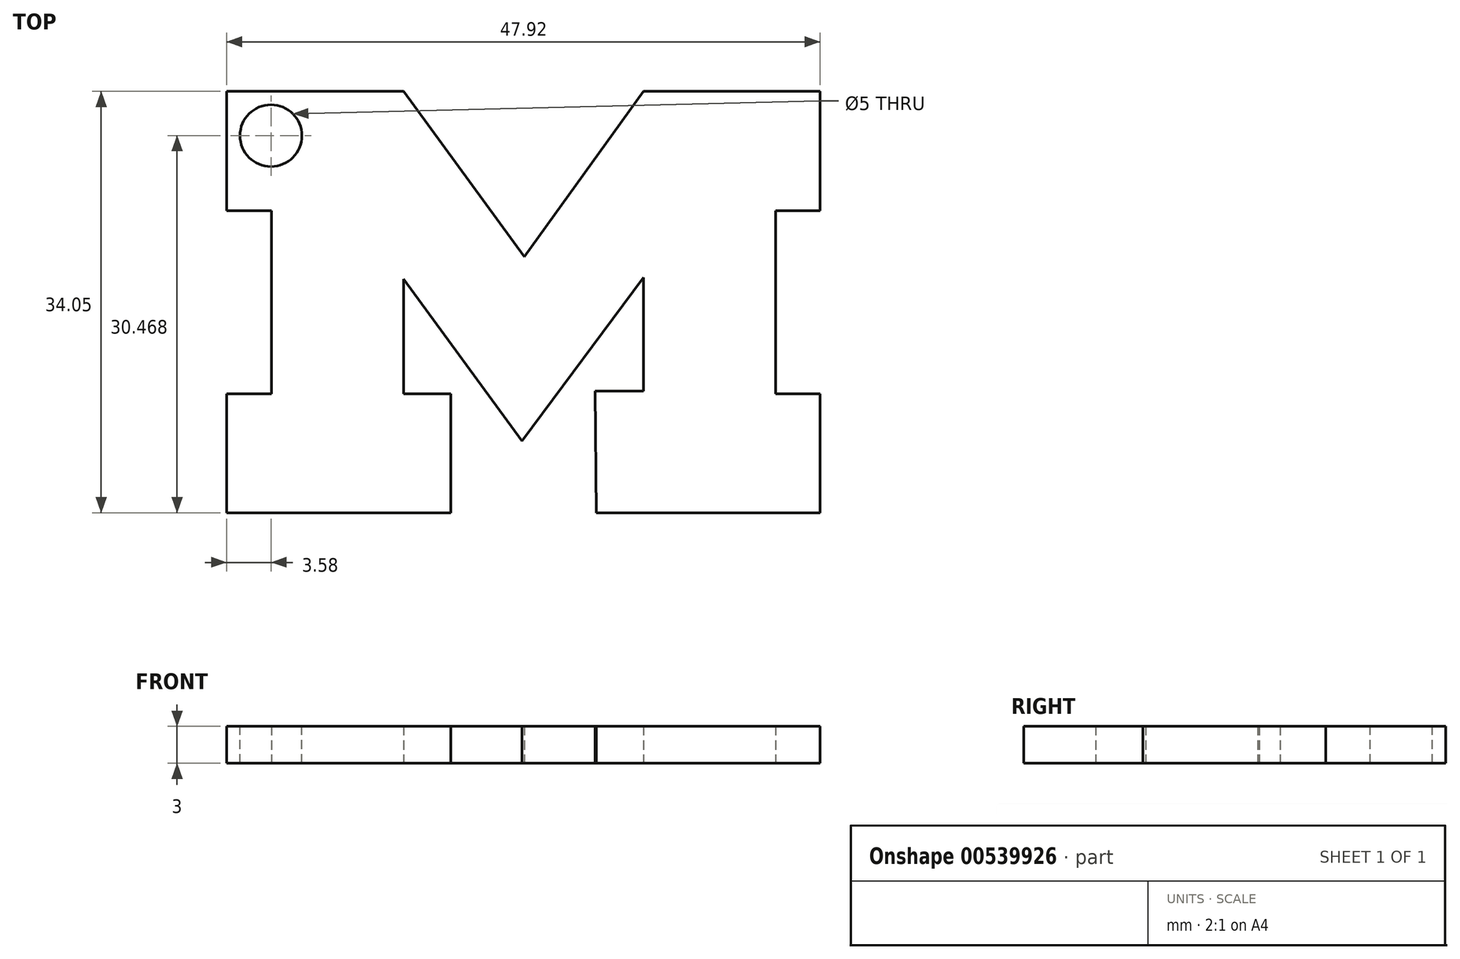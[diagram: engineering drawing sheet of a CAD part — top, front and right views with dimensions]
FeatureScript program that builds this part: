
annotation { "Feature Type Name" : "Feature", "Feature Type Description" : "" }
export const myFeature = defineFeature(function(context is Context, id is Id, definition is map)
    precondition{}
    {
        {
            var Q0;
            Q0=qCreatedBy(makeId("Top.planeOp"),FACE);
            var sketch = newSketch(context, id + "F0", { "sketchPlane" : qUnion([Q0])});
            skLineSegment(sketch, "E0", {"start": v(39.47, 27.3) * mm, "end": v(57.55, 27.3) * mm});
            skLineSegment(sketch, "E1", {"start": v(57.55, 27.3) * mm, "end": v(57.55, 36.88) * mm});
            skLineSegment(sketch, "E2", {"start": v(57.55, 36.88) * mm, "end": v(53.97, 36.88) * mm});
            skLineSegment(sketch, "E3", {"start": v(53.97, 36.88) * mm, "end": v(53.97, 51.68) * mm});
            skLineSegment(sketch, "E4", {"start": v(53.97, 51.68) * mm, "end": v(57.55, 51.68) * mm});
            skLineSegment(sketch, "E5", {"start": v(57.55, 51.68) * mm, "end": v(57.55, 61.34) * mm});
            skLineSegment(sketch, "E6", {"start": v(57.55, 61.34) * mm, "end": v(43.29, 61.34) * mm});
            skLineSegment(sketch, "E7", {"start": v(43.29, 61.34) * mm, "end": v(33.67, 48) * mm});
            skLineSegment(sketch, "E8", {"start": v(33.67, 48) * mm, "end": v(23.93, 61.34) * mm});
            skLineSegment(sketch, "E9", {"start": v(23.93, 61.34) * mm, "end": v(9.63, 61.34) * mm});
            skLineSegment(sketch, "E10", {"start": v(9.63, 61.34) * mm, "end": v(9.63, 51.68) * mm});
            skLineSegment(sketch, "E11", {"start": v(9.63, 51.68) * mm, "end": v(13.25, 51.68) * mm});
            skLineSegment(sketch, "E12", {"start": v(13.25, 51.68) * mm, "end": v(13.25, 36.88) * mm});
            skLineSegment(sketch, "E13", {"start": v(13.25, 36.88) * mm, "end": v(9.63, 36.88) * mm});
            skLineSegment(sketch, "E14", {"start": v(9.63, 36.88) * mm, "end": v(9.63, 27.3) * mm});
            skLineSegment(sketch, "E15", {"start": v(9.63, 27.3) * mm, "end": v(27.74, 27.3) * mm});
            skLineSegment(sketch, "E16", {"start": v(27.74, 27.3) * mm, "end": v(27.74, 36.88) * mm});
            skLineSegment(sketch, "E17", {"start": v(27.74, 36.88) * mm, "end": v(23.93, 36.88) * mm});
            skLineSegment(sketch, "E18", {"start": v(23.93, 36.88) * mm, "end": v(23.93, 46.16) * mm});
            skLineSegment(sketch, "E19", {"start": v(23.93, 46.16) * mm, "end": v(33.47, 33.1) * mm});
            skLineSegment(sketch, "E20", {"start": v(33.47, 33.1) * mm, "end": v(43.29, 46.28) * mm});
            skLineSegment(sketch, "E21", {"start": v(43.29, 46.28) * mm, "end": v(43.29, 37.12) * mm});
            skLineSegment(sketch, "E22", {"start": v(43.29, 37.12) * mm, "end": v(39.4, 37.12) * mm});
            skLineSegment(sketch, "E23", {"start": v(39.4, 37.12) * mm, "end": v(39.47, 27.3) * mm});
            skSolve(sketch);
        }
        {
            var Q0;
            Q0=makeQuery(id+"F0.imprint","IMPRINT",FACE,{"disambiguationData":[TD([[makeQuery(id+"F0.imprint","IMPRINT",EDGE,{"derivedFrom":sQuery(id+"F0.wireOp",EDGE,"E0")}),1.0]])]});
            extrude(context, id + "F1", {"entities" : qUnion([Q0]), "depth" : 3 * mm, "offsetDistance" : 25.4 * mm});
        }
        {
            var Q0;
            Q0=makeQuery(id+"F1.opExtrude","CAP_FACE",FACE,{"disambiguationData":[OSD([sQuery(id+"F0.wireOp",EDGE,"E0"),sQuery(id+"F0.wireOp",EDGE,"E1"),sQuery(id+"F0.wireOp",EDGE,"E2"),sQuery(id+"F0.wireOp",EDGE,"E3"),sQuery(id+"F0.wireOp",EDGE,"E4"),sQuery(id+"F0.wireOp",EDGE,"E5"),sQuery(id+"F0.wireOp",EDGE,"E6"),sQuery(id+"F0.wireOp",EDGE,"E7"),sQuery(id+"F0.wireOp",EDGE,"E8"),sQuery(id+"F0.wireOp",EDGE,"E9"),sQuery(id+"F0.wireOp",EDGE,"E10"),sQuery(id+"F0.wireOp",EDGE,"E11"),sQuery(id+"F0.wireOp",EDGE,"E12"),sQuery(id+"F0.wireOp",EDGE,"E13"),sQuery(id+"F0.wireOp",EDGE,"E14"),sQuery(id+"F0.wireOp",EDGE,"E15"),sQuery(id+"F0.wireOp",EDGE,"E16"),sQuery(id+"F0.wireOp",EDGE,"E17"),sQuery(id+"F0.wireOp",EDGE,"E18"),sQuery(id+"F0.wireOp",EDGE,"E19"),sQuery(id+"F0.wireOp",EDGE,"E20"),sQuery(id+"F0.wireOp",EDGE,"E21"),sQuery(id+"F0.wireOp",EDGE,"E22"),sQuery(id+"F0.wireOp",EDGE,"E23")])],"isStart":false});
            var sketch = newSketch(context, id + "F2", { "sketchPlane" : qUnion([Q0])});
            skCircle(sketch, "E24", {"center": v(13.2, 57.76) * mm, "radius": 2.5 * mm});
            skSolve(sketch);
        }
        {
            var Q0;
            Q0 = qSketchRegion(id + "F2", true);
            extrude(context, id + "F3", {"entities" : qUnion([Q0]), "operationType" : NewBodyOperationType.REMOVE, "oppositeDirection" : true, "depth" : 25.4 * mm, "offsetDistance" : 25.4 * mm});
        }
    });
